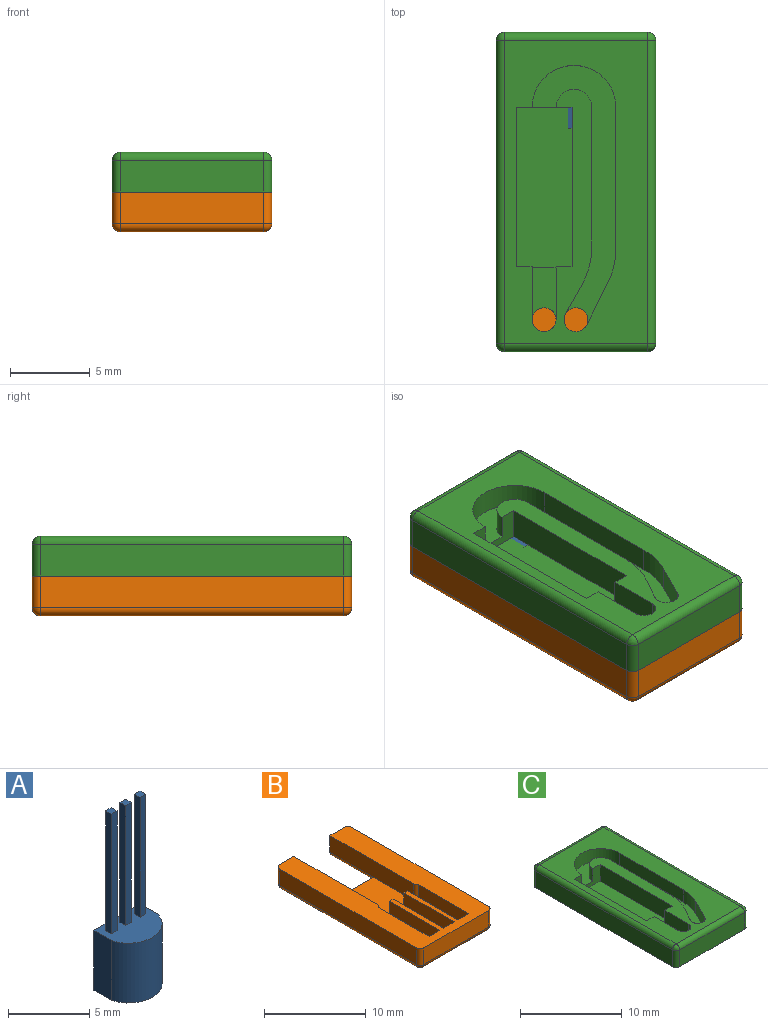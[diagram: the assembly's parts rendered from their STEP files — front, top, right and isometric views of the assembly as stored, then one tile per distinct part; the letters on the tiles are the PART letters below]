
ASSEMBLY  parts=3 mates=2
PART A: 21 faces, bbox 4x3.1x13.5 mm
  f0: plane 4x3.06mm, normal (0,0,1), area 9.9mm2, adj f1,f2,f3,f4,f6,f7,f8,f9
  f1: plane 4.5x1.5mm, normal (-1,0,0), area 6.7mm2, adj f0,f2,f4,f5
  f2: cylinder r=2.06mm len=4.5mm, axis (0,0,-1), area 24.6mm2, adj f0,f1,f3,f5
  f3: plane 4.5x1.5mm, normal (1,0,0), area 6.7mm2, adj f0,f2,f4,f5
  f4: plane 4.5x4mm, normal (0,1,0), area 18mm2, adj f0,f1,f3,f5
  f5: plane 4x3.06mm, normal (0,0,-1), area 10.6mm2, adj f1,f2,f3,f4
  f6: plane 9x0.5mm, normal (0,1,0), area 4.5mm2, adj f0,f7,f9,f10
  f7: plane 9x0.5mm, normal (-1,0,0), area 4.5mm2, adj f0,f6,f8,f10
  f8: plane 9x0.5mm, normal (0,-1,0), area 4.5mm2, adj f0,f7,f9,f10
  f9: plane 9x0.5mm, normal (1,0,0), area 4.5mm2, adj f0,f6,f8,f10
  f10: plane 0.5x0.5mm, normal (0,0,1), area 0.2mm2, adj f6,f7,f8,f9
  f11: plane 9x0.5mm, normal (-1,0,0), area 4.5mm2, adj f0,f12,f14,f15
  f12: plane 9x0.5mm, normal (0,-1,0), area 4.5mm2, adj f0,f11,f13,f15
  f13: plane 9x0.5mm, normal (1,0,0), area 4.5mm2, adj f0,f12,f14,f15
  f14: plane 9x0.5mm, normal (0,1,0), area 4.5mm2, adj f0,f11,f13,f15
  f15: plane 0.5x0.5mm, normal (0,0,1), area 0.2mm2, adj f11,f12,f13,f14
  f16: plane 9x0.5mm, normal (-1,0,0), area 4.5mm2, adj f0,f17,f19,f20
  f17: plane 9x0.5mm, normal (0,-1,0), area 4.5mm2, adj f0,f16,f18,f20
  f18: plane 9x0.5mm, normal (1,0,0), area 4.5mm2, adj f0,f17,f19,f20
  f19: plane 9x0.5mm, normal (0,1,0), area 4.5mm2, adj f0,f16,f18,f20
  f20: plane 0.5x0.5mm, normal (0,0,1), area 0.2mm2, adj f16,f17,f18,f19
PART B: 41 faces, bbox 10x20x2.5 mm
  f0: plane 20x10mm, normal (0,0,1), area 108.2mm2, adj f2,f3,f4,f5,f6,f7,f8,f10
  f1: plane 6x0.5mm, normal (0,1,0), area 2.6mm2, adj f9,f11,f26,f30
  f2: plane 19x2mm, normal (-1,0,0), area 38mm2, adj f0,f34,f38,f40
  f3: plane 9x2mm, normal (0,-1,0), area 18mm2, adj f0,f31,f37,f40
  f4: plane 19x2mm, normal (1,0,0), area 38mm2, adj f0,f27,f31,f32
  f5: plane 2x2mm, normal (0,1,0), area 4mm2, adj f0,f6,f27,f28
  f6: plane 12x2mm, normal (-1,0,0), area 23.4mm2, adj f0,f5,f10,f11,f23,f25,f26
  f7: plane 12x2mm, normal (1,0,0), area 23.4mm2, adj f0,f8,f10,f11,f19,f24,f30
  f8: plane 2x2mm, normal (0,1,0), area 4mm2, adj f0,f7,f33,f34
  f9: plane 19x9mm, normal (0,0,-1), area 138mm2, adj f1,f26,f28,f30,f32,f33,f37,f38
  f10: plane 5x2mm, normal (0,1,0), area 4mm2, adj f0,f6,f7,f11,f12,f14,f15,f18
  f11: plane 6x5mm, normal (0,0,1), area 30mm2, adj f1,f6,f7,f10
  f12: plane 7x1.5mm, normal (1,0,0), area 10.5mm2, adj f0,f10,f13,f15
  f13: plane 1.5x1.5mm, normal (0,1,0), area 2.2mm2, adj f0,f12,f14,f15
  f14: plane 7x1.5mm, normal (-1,0,0), area 10.5mm2, adj f0,f10,f13,f15
  f15: plane 7x1.5mm, normal (0,0,1), area 10.5mm2, adj f10,f12,f13,f14
  f16: plane 7x1.5mm, normal (1,0,0), area 10.5mm2, adj f0,f17,f19,f24
  f17: plane 1.5x1.5mm, normal (0,1,0), area 2.3mm2, adj f0,f16,f18,f19
  f18: plane 7x1.5mm, normal (-1,0,0), area 10.5mm2, adj f0,f10,f17,f19
  f19: plane 7.43x1.5mm, normal (0,0,1), area 10.5mm2, adj f7,f10,f16,f17,f18,f24
  f20: plane 7x1.5mm, normal (1,0,0), area 10.5mm2, adj f0,f10,f21,f23
  f21: plane 1.5x1.5mm, normal (0,1,0), area 2.2mm2, adj f0,f20,f22,f23
  f22: plane 7x1.5mm, normal (-1,0,0), area 10.5mm2, adj f0,f21,f23,f25
  f23: plane 7.43x1.5mm, normal (0,0,1), area 10.5mm2, adj f6,f10,f20,f21,f22,f25
  f24: cylinder r=0.5mm len=1.5mm, axis (0,0,-1), area 0.8mm2, adj f0,f7,f16,f19
  f25: cylinder r=0.5mm len=1.5mm, axis (0,0,-1), area 0.8mm2, adj f0,f6,f22,f23
  f26: cylinder r=0.5mm len=6mm, axis (0,-1,0), area 4.6mm2, adj f1,f6,f9,f28
  f27: cylinder r=0.5mm len=2mm, axis (0,0,-1), area 1.6mm2, adj f0,f4,f5,f29
  f28: cylinder r=0.5mm len=2mm, axis (-1,0,0), area 1.4mm2, adj f5,f9,f26,f29
  f29: sphere r=0.5mm, area 0.4mm2, adj f27,f28,f32
  f30: cylinder r=0.5mm len=6mm, axis (0,1,0), area 4.6mm2, adj f1,f7,f9,f33
  f31: cylinder r=0.5mm len=2mm, axis (0,0,-1), area 1.6mm2, adj f0,f3,f4,f35
  f32: cylinder r=0.5mm len=19mm, axis (0,1,0), area 14.9mm2, adj f4,f9,f29,f35
  f33: cylinder r=0.5mm len=2mm, axis (-1,0,0), area 1.4mm2, adj f8,f9,f30,f36
  f34: cylinder r=0.5mm len=2mm, axis (0,0,-1), area 1.6mm2, adj f0,f2,f8,f36
  f35: sphere r=0.5mm, area 0.4mm2, adj f31,f32,f37
  f36: sphere r=0.5mm, area 0.4mm2, adj f33,f34,f38
  f37: cylinder r=0.5mm len=9mm, axis (1,0,0), area 7.1mm2, adj f3,f9,f35,f39
  f38: cylinder r=0.5mm len=19mm, axis (0,-1,0), area 14.9mm2, adj f2,f9,f36,f39
  f39: sphere r=0.5mm, area 0.4mm2, adj f37,f38,f40
  f40: cylinder r=0.5mm len=2mm, axis (0,0,-1), area 1.6mm2, adj f0,f2,f3,f39
PART C: 38 faces, bbox 10x20x2.5 mm
  f0: plane 19x9mm, normal (0,0,1), area 100.1mm2, adj f1,f7,f8,f9,f10,f11,f16,f17
  f1: plane 3.5x2mm, normal (0,-1,0), area 4.7mm2, adj f0,f9,f11,f12,f29,f30,f37
  f2: plane 19x2mm, normal (-1,0,0), area 38mm2, adj f6,f15,f21,f24
  f3: plane 9x2mm, normal (0,-1,0), area 18mm2, adj f6,f18,f22,f24
  f4: plane 19x2mm, normal (1,0,0), area 38mm2, adj f6,f13,f17,f18
  f5: plane 9x2mm, normal (0,1,0), area 18mm2, adj f6,f13,f15,f16
  f6: plane 20x10mm, normal (0,0,-1), area 196.3mm2, adj f2,f3,f4,f5,f7,f8,f13,f15
  f7: cylinder r=0.75mm len=2.5mm, axis (0,0,1), area 8.2mm2, adj f0,f6,f25,f26,f27
  f8: cylinder r=0.75mm len=2.5mm, axis (0,0,1), area 8.5mm2, adj f0,f6,f34,f35,f37
  f9: plane 10x2mm, normal (1,0,0), area 20mm2, adj f0,f1,f10,f12
  f10: plane 3.5x2mm, normal (0,1,0), area 4.8mm2, adj f0,f9,f11,f12,f25,f26,f27
  f11: plane 10x2mm, normal (-1,0,0), area 20mm2, adj f0,f1,f10,f12
  f12: plane 10x3.5mm, normal (0,0,1), area 35mm2, adj f1,f9,f10,f11
  f13: cylinder r=0.5mm len=2mm, axis (0,0,1), area 1.6mm2, adj f4,f5,f6,f14
  f14: sphere r=0.5mm, area 0.4mm2, adj f13,f16,f17
  f15: cylinder r=0.5mm len=2mm, axis (0,0,-1), area 1.6mm2, adj f2,f5,f6,f19
  f16: cylinder r=0.5mm len=9mm, axis (1,0,0), area 7.1mm2, adj f0,f5,f14,f19
  f17: cylinder r=0.5mm len=19mm, axis (0,-1,0), area 14.9mm2, adj f0,f4,f14,f20
  f18: cylinder r=0.5mm len=2mm, axis (0,0,-1), area 1.6mm2, adj f3,f4,f6,f20
  f19: sphere r=0.5mm, area 0.4mm2, adj f15,f16,f21
  f20: sphere r=0.5mm, area 0.4mm2, adj f17,f18,f22
  f21: cylinder r=0.5mm len=19mm, axis (0,1,0), area 14.9mm2, adj f0,f2,f19,f23
  f22: cylinder r=0.5mm len=9mm, axis (-1,0,0), area 7.1mm2, adj f0,f3,f20,f23
  f23: sphere r=0.5mm, area 0.4mm2, adj f21,f22,f24
  f24: cylinder r=0.5mm len=2mm, axis (0,0,1), area 1.6mm2, adj f2,f3,f6,f23
  f25: plane 3.3x1.5mm, normal (-1,0,0), area 4.9mm2, adj f0,f7,f10,f27
  f26: plane 3.3x1.5mm, normal (1,0,0), area 4.9mm2, adj f0,f7,f10,f27
  f27: plane 3.3x1.5mm, normal (0,0,1), area 4.1mm2, adj f7,f10,f25,f26
  f28: plane 8.81x1.5mm, normal (-1,0,0), area 13.2mm2, adj f0,f29,f36,f37
  f29: cylinder r=2.62mm len=5.25mm, axis (0,0,1), area 12.4mm2, adj f0,f1,f28,f37
  f30: cylinder r=1.12mm len=2.25mm, axis (0,0,1), area 5.3mm2, adj f0,f1,f31,f37
  f31: plane 8.69x1.5mm, normal (1,0,0), area 13mm2, adj f0,f30,f32,f37
  f32: cylinder r=5mm len=2.46mm, axis (0,0,1), area 3.9mm2, adj f0,f31,f33,f37
  f33: plane 1.66x1.5mm, normal (0.87,-0.49,0), area 2.9mm2, adj f0,f32,f34,f37
  f34: plane 1.5x0.01mm, normal (0.55,0.83,0), area 0mm2, adj f0,f8,f33,f37
  f35: plane 2.57x1.5mm, normal (-0.89,0.45,0), area 4.3mm2, adj f0,f8,f36,f37
  f36: cylinder r=5mm len=2.25mm, axis (0,0,1), area 3.5mm2, adj f0,f28,f35,f37
  f37: plane 16.26x5.25mm, normal (0,0,1), area 28.3mm2, adj f1,f8,f28,f29,f30,f31,f32,f33
PLACE A rot(axis=(0,-0.71,0.71),180deg) t=(-4.13,11.33,5.8)mm
PLACE B t=(-11.13,-7.17,5.8)mm
PLACE C t=(-11.13,-7.17,8.3)mm
MATE fastened B.f0 <-> C.f6  axis (0,0,1) through (-6.13,-7.17,8.3)mm
MATE fastened A.f0 <-> B.f1  axis (0,-1,0) through (-6.13,6.83,6.3)mm
